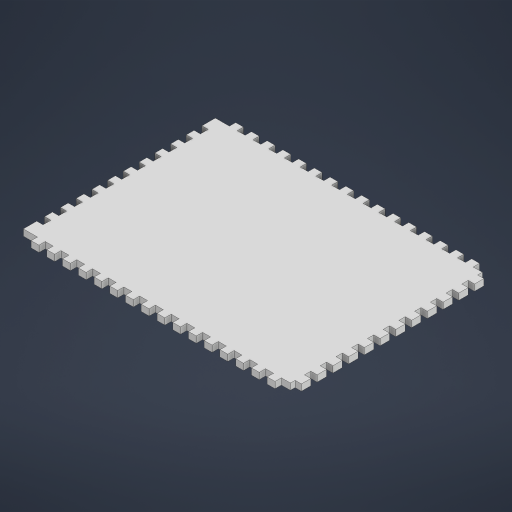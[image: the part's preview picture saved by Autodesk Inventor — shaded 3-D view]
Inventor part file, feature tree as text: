
AUTODESK INVENTOR PART (.ipt)
format: ipt  version: 2023 (Build 270158030, 158C)  size: 793,088 bytes
history: native  units: mm
features: move_body x5, direct_edit x4, sketch x4, extrude x3, mirror x1, delete_face x1, projected_geometry x1
ambient origin geometry x8: Origin, YZ Plane, XZ Plane, XY Plane, X Axis, Y Axis, Z Axis, Center Point
bodies: Solid1 (feature_tree)
feature tree (19):
  extrude  "Extrusion1"  Depth=4.0mm TaperAngle=0.0deg
  direct_edit  "Direct Edit1"
  mirror  "Mirror1"
  direct_edit  "Direct Edit2"
  extrude  "Extrusion2"  Depth=0.75mm TaperAngle=0.0deg
  direct_edit  "Direct Edit3"
  extrude  "Extrusion3"  Depth=4.0mm
  delete_face  "Delete Face1"
  direct_edit  "Direct Edit4"
  sketch  "Sketch4"  dims[d18=70.0mm d20=10.0mm d21=70.0mm d23=10.0mm d26=4.0mm d27=0.0mm d28=0.0mm d29=0.0mm d30=-4.0mm d31=0.0mm d32=0.0mm d33=-4.0mm d34=4.0mm d35=5.0mm d36=60.0mm d38=10.0mm d39=60.0mm d41=10.0mm d44=4.25mm d45=0.0mm d46=0.0mm d47=0.0mm d48=-0.75mm]
  sketch  "Sketch1"  dims[d1=160.0mm d3=10.0mm d4=5.0mm d5=4.0mm d6=10.0mm d7=10.0mm d8=4.0mm d9=0.0mm]
  sketch  "Sketch2"  dims[d10=0.0mm d11=0.0mm d12=0.75mm d13=0.0mm d14=0.0mm d15=0.75mm]
  sketch  "Sketch3"  dims[d16=4.0mm d17=4.0mm]
  projected_geometry  "Projected Loop1"
  move_body  "Move1"
  move_body  "Move2"
  move_body  "Move3"
  move_body  "Move4"
  move_body  "Move5"
